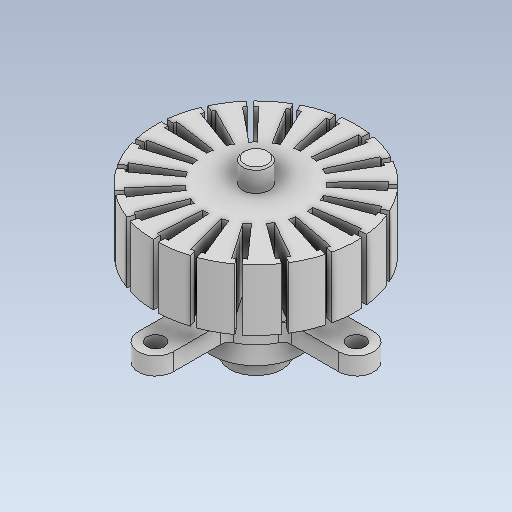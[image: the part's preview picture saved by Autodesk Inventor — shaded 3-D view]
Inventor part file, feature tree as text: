
AUTODESK INVENTOR PART (.ipt)
format: ipt  version: 2023 (Build 270158000, 158)  size: 415,232 bytes
history: native  units: mm
features: sketch x8, other x3, plane x1
ambient origin geometry x8: Origin, YZ Plane, XZ Plane, XY Plane, X Axis, Y Axis, Z Axis, Center Point
bodies: Solid1 (feature_tree)
feature tree (12):
  other  "mot_27_2.ipt"
  other  "Solid1::mot_27_2.ipt"
  other  "TaggingFeature1"
  sketch  "Sketch1"  dims[d0=10.0mm]
  sketch  "Sketch2"
  sketch  "Sketch3"
  sketch  "Sketch4"
  sketch  "Sketch5"
  sketch  "Sketch6"
  sketch  "Sketch7"
  sketch  "Sketch8"
  plane  "Work Plane1"
